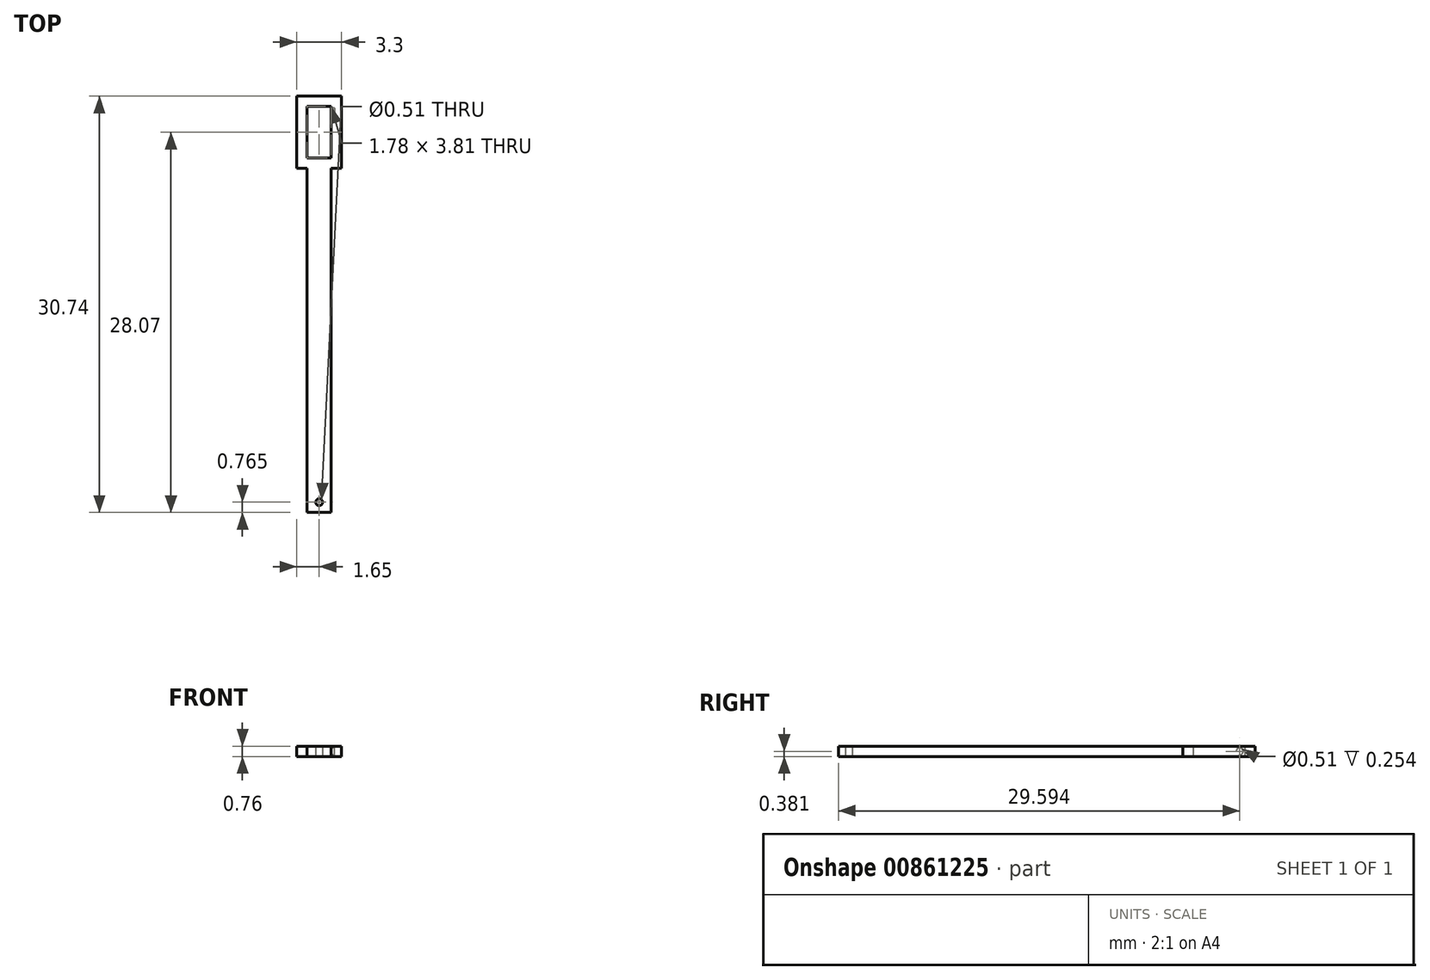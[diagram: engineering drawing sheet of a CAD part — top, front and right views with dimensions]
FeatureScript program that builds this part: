
annotation { "Feature Type Name" : "Feature", "Feature Type Description" : "" }
export const myFeature = defineFeature(function(context is Context, id is Id, definition is map)
    precondition{}
    {
        {
            var Q0;
            Q0=qCreatedBy(makeId("Top.planeOp"),FACE);
            var sketch = newSketch(context, id + "F0", { "sketchPlane" : qUnion([Q0])});
            skLineSegment(sketch, "E0.bottom", {"start": v(1.65, -2.67) * mm, "end": v(0.89, -2.67) * mm});
            skLineSegment(sketch, "E0.top", {"start": v(1.65, 2.67) * mm, "end": v(-1.65, 2.67) * mm});
            skLineSegment(sketch, "E0.left", {"start": v(1.65, -2.67) * mm, "end": v(1.65, 2.67) * mm});
            skLineSegment(sketch, "E0.right", {"start": v(-1.65, -2.67) * mm, "end": v(-1.65, 2.67) * mm});
            skPoint(sketch, "E0.middle", {"position": v(0, 0) * mm});
            skLineSegment(sketch, "E1.bottom", {"start": v(0.89, -1.9) * mm, "end": v(-0.89, -1.9) * mm});
            skLineSegment(sketch, "E1.top", {"start": v(0.89, 1.9) * mm, "end": v(-0.89, 1.9) * mm});
            skLineSegment(sketch, "E1.left", {"start": v(0.89, -1.9) * mm, "end": v(0.89, 1.9) * mm});
            skLineSegment(sketch, "E1.right", {"start": v(-0.89, -1.9) * mm, "end": v(-0.89, 1.9) * mm});
            skLineSegment(sketch, "E2", {"start": v(-0.89, -2.67) * mm, "end": v(-0.89, -28.07) * mm});
            skLineSegment(sketch, "E3", {"start": v(-0.89, -28.07) * mm, "end": v(0.89, -28.07) * mm});
            skLineSegment(sketch, "E4", {"start": v(0.89, -2.67) * mm, "end": v(0.89, -28.07) * mm});
            skLineSegment(sketch, "E5.trimOffspring", {"start": v(-0.89, -2.67) * mm, "end": v(-1.65, -2.67) * mm});
            skCircle(sketch, "E6", {"center": v(0, -27.3) * mm, "radius": 0.25 * mm});
            skSolve(sketch);
        }
        {
            var Q0;
            Q0 = qSketchRegion(id + "F0", true);
            extrude(context, id + "F1", {"entities" : qUnion([Q0]), "depth" : 0.76 * mm, "offsetDistance" : 25.4 * mm});
        }
        {
            var Q0;
            Q0=qCreatedBy(makeId("Right.planeOp"),FACE);
            cPlane(context, id + "F2", {"entities" : qUnion([Q0]), "cplaneType" : CPlaneType.OFFSET, "offset" : 0.89 * mm, "width" : 152.4 * mm, "height" : 152.4 * mm});
        }
        {
            var Q0;
            Q0=qCreatedBy(id+"F2.planeOp",FACE);
            var sketch = newSketch(context, id + "F3", { "sketchPlane" : qUnion([Q0])});
            skCircle(sketch, "E7", {"center": v(1.52, 0.38) * mm, "radius": 0.25 * mm});
            skSolve(sketch);
        }
        {
            var Q0;
            Q0 = qSketchRegion(id + "F3", true);
            var Q1;
            Q1=makeQuery(id+"F1.opExtrude","SWEPT_FACE",FACE,{"disambiguationData":[OSD([sQuery(id+"F0.wireOp",EDGE,"E0.left")])]});
            extrude(context, id + "F4", {"entities" : qUnion([Q0, Q1]), "operationType" : NewBodyOperationType.REMOVE, "depth" : 0.25 * mm, "offsetDistance" : 25.4 * mm});
        }
    });
